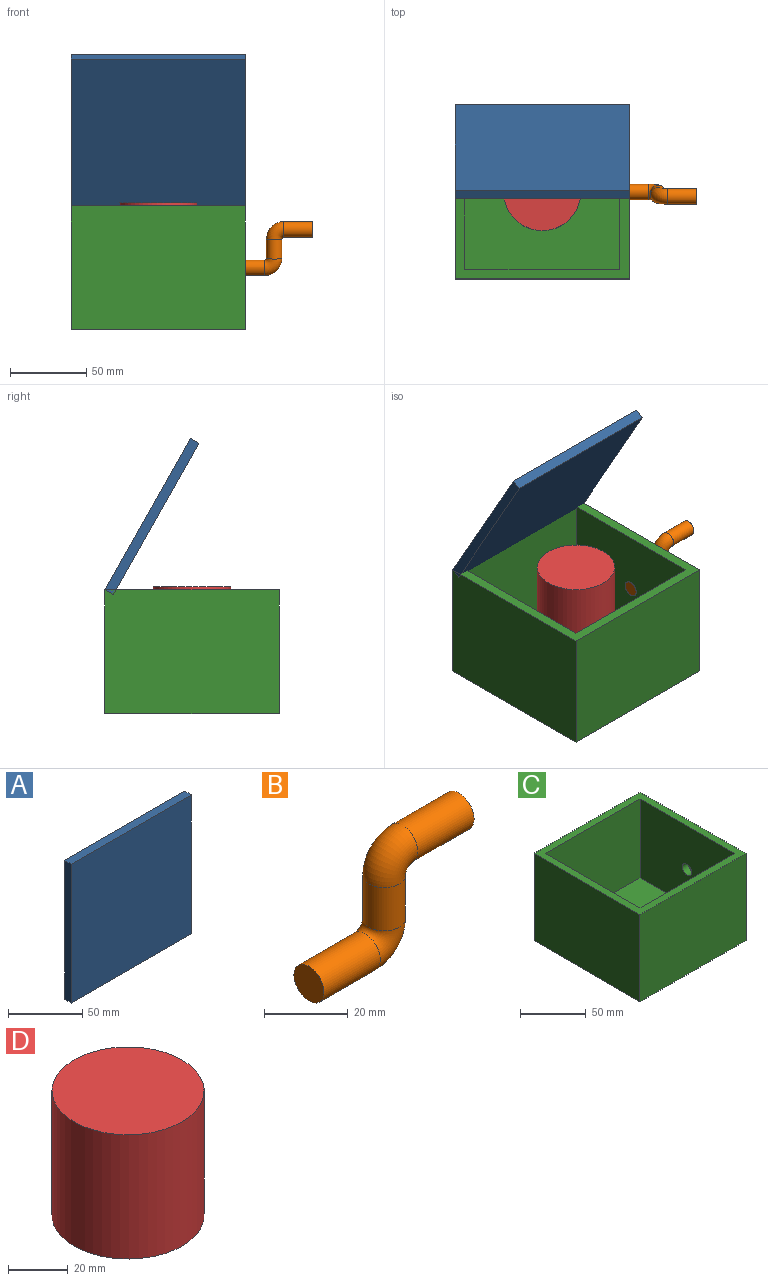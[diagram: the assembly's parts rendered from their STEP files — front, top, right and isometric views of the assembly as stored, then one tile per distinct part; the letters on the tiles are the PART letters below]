
ASSEMBLY  parts=4 mates=3
PART A: 6 faces, bbox 114.3x6.4x114.3 mm
  f0: plane 114.3x114.3mm, normal (0,-1,0), area 13064.5mm2, adj f1,f3,f4,f5
  f1: plane 114.3x6.35mm, normal (1,0,0), area 725.8mm2, adj f0,f2,f4,f5
  f2: plane 114.3x114.3mm, normal (0,1,0), area 13064.5mm2, adj f1,f3,f4,f5
  f3: plane 114.3x6.35mm, normal (-1,0,0), area 725.8mm2, adj f0,f2,f4,f5
  f4: plane 114.3x6.35mm, normal (0,0,1), area 725.8mm2, adj f0,f1,f2,f3
  f5: plane 114.3x6.35mm, normal (0,0,-1), area 725.8mm2, adj f0,f1,f2,f3
PART B: 7 faces, bbox 50.8x10.2x37.4 mm
  f0: plane 10.16x10.16mm, normal (1,0,0), area 81.1mm2, adj f2
  f1: plane 10.16x10.16mm, normal (-1,0,0), area 81.1mm2, adj f6
  f2: cylinder r=5.08mm len=19.05mm, axis (-1,0,0), area 608mm2, adj f0,f3
  f3: torus R=6.35mm, axis (0,-1,0), area 318.4mm2, adj f2,f4
  f4: cylinder r=5.08mm len=12.7mm, axis (0,0,-1), area 405.4mm2, adj f3,f5
  f5: torus R=6.35mm, axis (0,1,0), area 318.4mm2, adj f4,f6
  f6: cylinder r=5.08mm len=19.05mm, axis (-1,0,0), area 608mm2, adj f1,f5
PART C: 12 faces, bbox 114.3x114.3x81.3 mm
  f0: plane 114.3x114.3mm, normal (0,0,1), area 2741.9mm2, adj f1,f2,f3,f4,f6,f7,f8,f9
  f1: plane 114.3x81.28mm, normal (0,1,0), area 9290.3mm2, adj f0,f2,f4,f5
  f2: plane 114.3x81.28mm, normal (-1,0,0), area 9290.3mm2, adj f0,f1,f3,f5
  f3: plane 114.3x81.28mm, normal (0,-1,0), area 9290.3mm2, adj f0,f2,f4,f5
  f4: plane 114.3x81.28mm, normal (1,0,0), area 9209.2mm2, adj f0,f1,f3,f5,f11
  f5: plane 114.3x114.3mm, normal (0,0,-1), area 13064.5mm2, adj f1,f2,f3,f4
  f6: plane 101.6x73.66mm, normal (-1,0,0), area 7402.8mm2, adj f0,f7,f9,f10,f11
  f7: plane 101.6x73.66mm, normal (0,-1,0), area 7483.9mm2, adj f0,f6,f8,f10
  f8: plane 101.6x73.66mm, normal (1,0,0), area 7483.9mm2, adj f0,f7,f9,f10
  f9: plane 101.6x73.66mm, normal (0,1,0), area 7483.9mm2, adj f0,f6,f8,f10
  f10: plane 101.6x101.6mm, normal (0,0,1), area 10322.6mm2, adj f6,f7,f8,f9
  f11: cylinder r=5.08mm len=10.16mm, axis (1,0,0), area 202.7mm2, adj f4,f6
PART D: 3 faces, bbox 50.8x50.8x50.8 mm
  f0: cylinder r=25.4mm len=50.8mm, axis (0,0,-1), area 8107.3mm2, adj f1,f2
  f1: plane 50.8x50.8mm, normal (0,0,1), area 2026.8mm2, adj f0
  f2: plane 50.8x50.8mm, normal (0,0,-1), area 2026.8mm2, adj f0
PLACE A rot(axis=(1,0,0),29.4deg) t=(0,48.15,-20.72)mm
PLACE B rot(axis=(1,0,0),6.6deg) t=(52.99,1.63,81.75)mm
PLACE C at identity fixed
PLACE D t=(-0.69,-1.78,32.56)mm
MATE revolute B.f6 <-> C.f11  axis (-1,0,0) through (44.45,6.35,40.64)mm
MATE revolute A.f3 <-> C.f2  axis (-1,0,0) through (-63.5,63.5,81.28)mm
MATE slider D.f0 <-> C.f10  axis (0,0,-1) through (-6.35,6.35,32.56)mm
